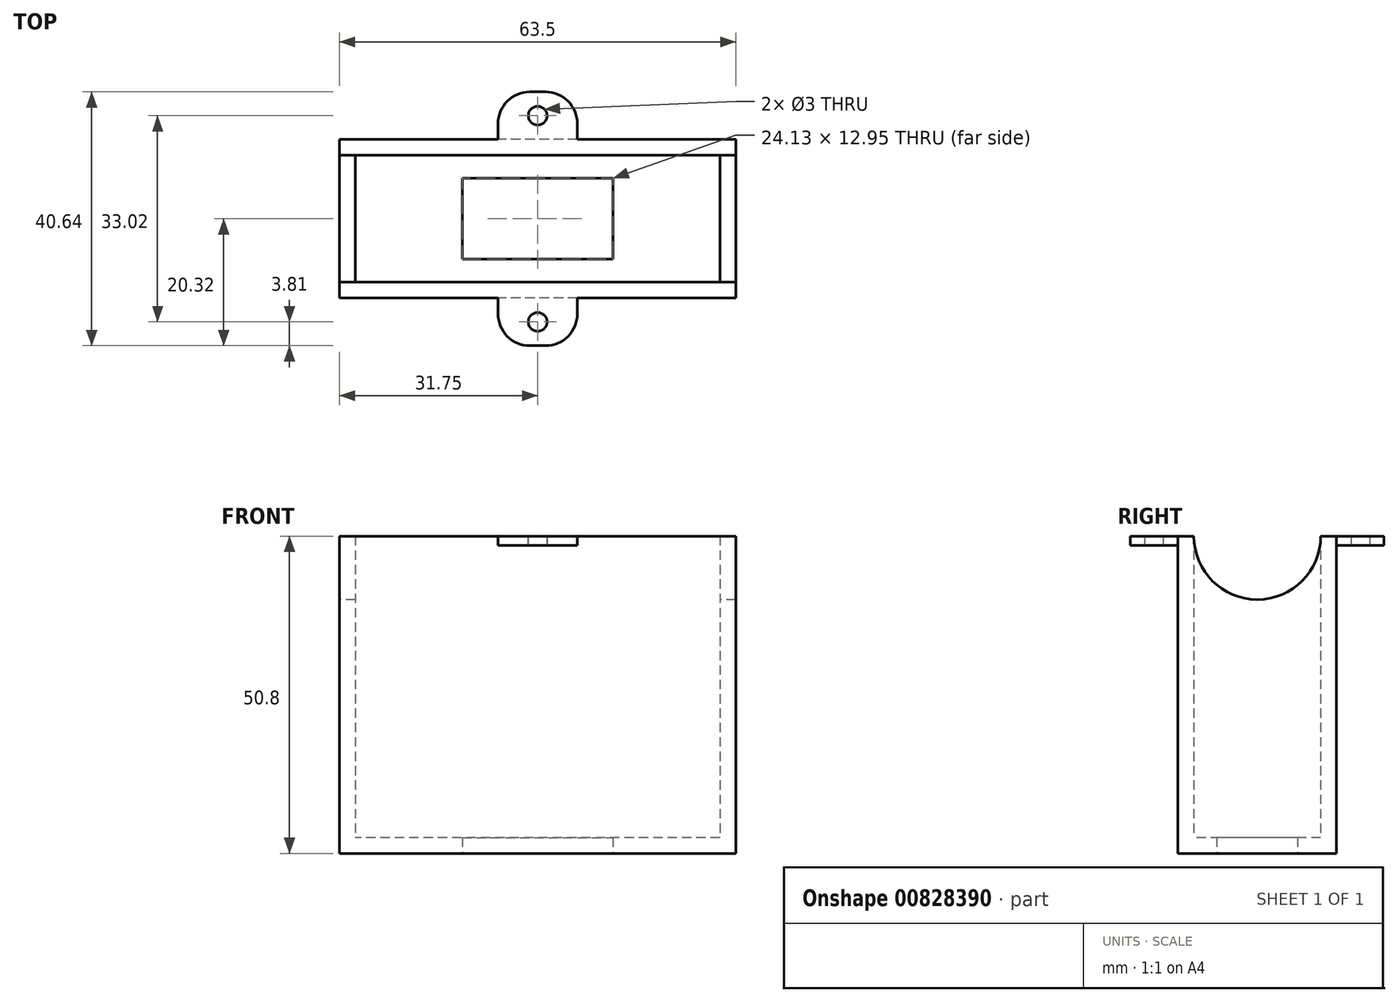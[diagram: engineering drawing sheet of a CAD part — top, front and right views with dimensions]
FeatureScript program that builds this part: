
annotation { "Feature Type Name" : "Feature", "Feature Type Description" : "" }
export const myFeature = defineFeature(function(context is Context, id is Id, definition is map)
    precondition{}
    {
        {
            var Q0;
            Q0=qCreatedBy(makeId("Top.planeOp"),FACE);
            var sketch = newSketch(context, id + "F0", { "sketchPlane" : qUnion([Q0])});
            skLineSegment(sketch, "E0.bottom", {"start": v(31.75, 12.7) * mm, "end": v(-31.75, 12.7) * mm});
            skLineSegment(sketch, "E0.top", {"start": v(31.75, -12.7) * mm, "end": v(-31.75, -12.7) * mm});
            skLineSegment(sketch, "E0.left", {"start": v(31.75, 12.7) * mm, "end": v(31.75, -12.7) * mm});
            skLineSegment(sketch, "E0.right", {"start": v(-31.75, 12.7) * mm, "end": v(-31.75, -12.7) * mm});
            skPoint(sketch, "E0.middle", {"position": v(0, 0) * mm});
            skLineSegment(sketch, "E1.bottom", {"start": v(29.21, 10.16) * mm, "end": v(-29.21, 10.16) * mm});
            skLineSegment(sketch, "E1.top", {"start": v(29.21, -10.16) * mm, "end": v(-29.21, -10.16) * mm});
            skLineSegment(sketch, "E1.left", {"start": v(29.21, 10.16) * mm, "end": v(29.21, -10.16) * mm});
            skLineSegment(sketch, "E1.right", {"start": v(-29.21, 10.16) * mm, "end": v(-29.21, -10.16) * mm});
            skSolve(sketch);
        }
        {
            var Q0;
            Q0 = qSketchRegion(id + "F0", true);
            extrude(context, id + "F1", {"entities" : qUnion([Q0]), "depth" : 50.8 * mm, "offsetDistance" : 25.4 * mm});
        }
        {
            var Q0;
            Q0=makeQuery(id+"F1.opExtrude","CAP_FACE",FACE,{"disambiguationData":[OSD([sQuery(id+"F0.wireOp",EDGE,"E0.bottom"),sQuery(id+"F0.wireOp",EDGE,"E0.top"),sQuery(id+"F0.wireOp",EDGE,"E0.left"),sQuery(id+"F0.wireOp",EDGE,"E0.right"),sQuery(id+"F0.wireOp",EDGE,"E1.bottom"),sQuery(id+"F0.wireOp",EDGE,"E1.top"),sQuery(id+"F0.wireOp",EDGE,"E1.left"),sQuery(id+"F0.wireOp",EDGE,"E1.right")])],"isStart":true});
            var sketch = newSketch(context, id + "F2", { "sketchPlane" : qUnion([Q0])});
            skLineSegment(sketch, "E2.bottom", {"start": v(29.21, -10.16) * mm, "end": v(-29.21, -10.16) * mm});
            skLineSegment(sketch, "E2.top", {"start": v(29.21, 10.16) * mm, "end": v(-29.21, 10.16) * mm});
            skLineSegment(sketch, "E2.left", {"start": v(29.21, -10.16) * mm, "end": v(29.21, 10.16) * mm});
            skLineSegment(sketch, "E2.right", {"start": v(-29.21, -10.16) * mm, "end": v(-29.21, 10.16) * mm});
            skPoint(sketch, "E2.middle", {"position": v(0, 0) * mm});
            skSolve(sketch);
        }
        {
            var Q0;
            Q0 = qSketchRegion(id + "F2", true);
            extrude(context, id + "F3", {"entities" : qUnion([Q0]), "operationType" : NewBodyOperationType.ADD, "oppositeDirection" : true, "depth" : 2.54 * mm, "offsetDistance" : 25.4 * mm});
        }
        {
            var Q0;
            Q0=makeQuery(id+"F1.opExtrude","SWEPT_FACE",FACE,{"disambiguationData":[OSD([sQuery(id+"F0.wireOp",EDGE,"E0.right")])]});
            var sketch = newSketch(context, id + "F4", { "sketchPlane" : qUnion([Q0])});
            skCircle(sketch, "E3", {"center": v(0, 50.8) * mm, "radius": 10.16 * mm});
            skSolve(sketch);
        }
        {
            var Q0;
            Q0 = qSketchRegion(id + "F4", true);
            extrude(context, id + "F5", {"entities" : qUnion([Q0]), "operationType" : NewBodyOperationType.REMOVE, "endBound" : BoundingType.THROUGH_ALL, "oppositeDirection" : true, "depth" : 25.4 * mm, "offsetDistance" : 25.4 * mm});
        }
        {
            var Q0;
            Q0=makeQuery(id+"F3.boolean.opBoolean","MERGE",FACE,{"derivedFrom":[makeQuery(id+"F1.opExtrude","CAP_FACE",FACE,{"disambiguationData":[OSD([sQuery(id+"F0.wireOp",EDGE,"E0.bottom"),sQuery(id+"F0.wireOp",EDGE,"E0.top"),sQuery(id+"F0.wireOp",EDGE,"E0.left"),sQuery(id+"F0.wireOp",EDGE,"E0.right"),sQuery(id+"F0.wireOp",EDGE,"E1.bottom"),sQuery(id+"F0.wireOp",EDGE,"E1.top"),sQuery(id+"F0.wireOp",EDGE,"E1.left"),sQuery(id+"F0.wireOp",EDGE,"E1.right")])],"isStart":true}),makeQuery(id+"F3.opExtrude","CAP_FACE",FACE,{"disambiguationData":[OSD([sQuery(id+"F2.wireOp",EDGE,"E2.bottom"),sQuery(id+"F2.wireOp",EDGE,"E2.top"),sQuery(id+"F2.wireOp",EDGE,"E2.left"),sQuery(id+"F2.wireOp",EDGE,"E2.right")])],"isStart":true})]});
            var sketch = newSketch(context, id + "F6", { "sketchPlane" : qUnion([Q0])});
            skLineSegment(sketch, "E4.bottom", {"start": v(-12.06, -6.48) * mm, "end": v(12.07, -6.48) * mm});
            skLineSegment(sketch, "E4.top", {"start": v(-12.07, 6.48) * mm, "end": v(12.06, 6.48) * mm});
            skLineSegment(sketch, "E4.left", {"start": v(-12.06, -6.48) * mm, "end": v(-12.07, 6.48) * mm});
            skLineSegment(sketch, "E4.right", {"start": v(12.07, -6.48) * mm, "end": v(12.06, 6.48) * mm});
            skPoint(sketch, "E4.middle", {"position": v(0, 0) * mm});
            skSolve(sketch);
        }
        {
            var Q0;
            Q0=makeQuery(id+"F1.opExtrude","SWEPT_FACE",FACE,{"disambiguationData":[OSD([sQuery(id+"F0.wireOp",EDGE,"E0.top")])]});
            var sketch = newSketch(context, id + "F7", { "sketchPlane" : qUnion([Q0])});
            skLineSegment(sketch, "E5.bottom", {"start": v(6.35, 50.8) * mm, "end": v(-6.35, 50.8) * mm});
            skLineSegment(sketch, "E5.top", {"start": v(6.35, 49.3) * mm, "end": v(-6.35, 49.3) * mm});
            skLineSegment(sketch, "E5.left", {"start": v(6.35, 50.8) * mm, "end": v(6.35, 49.3) * mm});
            skLineSegment(sketch, "E5.right", {"start": v(-6.35, 50.8) * mm, "end": v(-6.35, 49.3) * mm});
            skPoint(sketch, "E5.middle", {"position": v(0, 50.05) * mm});
            skSolve(sketch);
        }
        {
            var Q0;
            Q0 = qSketchRegion(id + "F7", true);
            extrude(context, id + "F8", {"entities" : qUnion([Q0]), "operationType" : NewBodyOperationType.ADD, "depth" : 7.62 * mm, "offsetDistance" : 25.4 * mm});
        }
        {
            var Q0;
            Q0=makeQuery(id+"F1.opExtrude","SWEPT_BODY",BODY,{"disambiguationData":[OSD([sQuery(id+"F0.wireOp",EDGE,"E0.bottom"),sQuery(id+"F0.wireOp",EDGE,"E0.top"),sQuery(id+"F0.wireOp",EDGE,"E0.left"),sQuery(id+"F0.wireOp",EDGE,"E0.right"),sQuery(id+"F0.wireOp",EDGE,"E1.bottom"),sQuery(id+"F0.wireOp",EDGE,"E1.top"),sQuery(id+"F0.wireOp",EDGE,"E1.left"),sQuery(id+"F0.wireOp",EDGE,"E1.right")])]});
            var Q1;
            Q1=qCreatedBy(makeId("Front.planeOp"),FACE);
            mirror(context, id + "F9", {"operationType" : NewBodyOperationType.ADD, "entities" : qUnion([Q0]), "mirrorPlane" : qUnion([Q1])});
        }
        {
            var Q0;
            {var subQ0=sQuery(id+"F0.wireOp",EDGE,"E1.top");var subQ1=sQuery(id+"F0.wireOp",EDGE,"E0.right");var subQ2=sQuery(id+"F0.wireOp",EDGE,"E0.left");var subQ3=sQuery(id+"F0.wireOp",EDGE,"E0.top");var subQ4=sQuery(id+"F0.wireOp",EDGE,"E1.left");var subQ5=sQuery(id+"F0.wireOp",EDGE,"E1.right");Q0=makeQuery(id+"F8.boolean.opBoolean","MERGE",FACE,{"derivedFrom":[makeQuery(id+"F5.boolean.opBoolean","SPLIT",FACE,{"disambiguationData":[TD([makeQuery(id+"F1.opExtrude","SWEPT_FACE",FACE,{"disambiguationData":[OSD([subQ3])]})])],"derivedFrom":makeQuery(id+"F1.opExtrude","CAP_FACE",FACE,{"disambiguationData":[OSD([sQuery(id+"F0.wireOp",EDGE,"E0.bottom"),subQ3,subQ2,subQ1,sQuery(id+"F0.wireOp",EDGE,"E1.bottom"),subQ0,subQ4,subQ5])],"isStart":false})}),makeQuery(id+"F8.opExtrude","SWEPT_FACE",FACE,{"disambiguationData":[OSD([sQuery(id+"F7.wireOp",EDGE,"E5.bottom")])]})]});}
            var sketch = newSketch(context, id + "F10", { "sketchPlane" : qUnion([Q0])});
            skCircle(sketch, "E6", {"center": v(0, -16.51) * mm, "radius": 1.5 * mm});
            skPoint(sketch, "E6.centerSnap0", {"position": v(6.35, -16.51) * mm});
            skPoint(sketch, "E6.centerSnap1", {"position": v(0, -20.32) * mm});
            skSolve(sketch);
        }
        {
            var Q0;
            Q0 = qSketchRegion(id + "F10", true);
            extrude(context, id + "F11", {"entities" : qUnion([Q0]), "operationType" : NewBodyOperationType.REMOVE, "oppositeDirection" : true, "depth" : 25.4 * mm, "offsetDistance" : 25.4 * mm});
        }
        {
            var Q0;
            Q0=makeQuery(id+"F9.opPattern","COPY",FACE,{"derivedFrom":makeQuery(id+"F8.opExtrude","SWEPT_FACE",FACE,{"disambiguationData":[OSD([sQuery(id+"F7.wireOp",EDGE,"E5.top")])]}),"instanceName":"1"});
            var sketch = newSketch(context, id + "F12", { "sketchPlane" : qUnion([Q0])});
            skCircle(sketch, "E7", {"center": v(0, -16.51) * mm, "radius": 1.5 * mm});
            skPoint(sketch, "E8", {"position": v(6.35, -16.51) * mm});
            skLineSegment(sketch, "E9", {"start": v(6.35, -16.51) * mm, "end": v(0, -16.51) * mm});
            skSolve(sketch);
        }
        {
            var Q0;
            Q0=makeQuery(id+"F12.imprint","IMPRINT",FACE,{"disambiguationData":[TD([[makeQuery(id+"F12.imprint","IMPRINT",EDGE,{"derivedFrom":sQuery(id+"F12.wireOp",EDGE,"E7")}),1.0]])]});
            extrude(context, id + "F13", {"entities" : qUnion([Q0]), "operationType" : NewBodyOperationType.REMOVE, "oppositeDirection" : true, "depth" : 25.4 * mm, "offsetDistance" : 25.4 * mm});
        }
        {
            var Q0;
            Q0=makeQuery(id+"F9.opPattern","COPY",EDGE,{"derivedFrom":makeQuery(id+"F8.opExtrude","CAP_EDGE",EDGE,{"disambiguationData":[OSD([sQuery(id+"F7.wireOp",EDGE,"E5.left")])],"isStart":false}),"instanceName":"1"});
            var Q1;
            Q1=makeQuery(id+"F9.opPattern","COPY",EDGE,{"derivedFrom":makeQuery(id+"F8.opExtrude","CAP_EDGE",EDGE,{"disambiguationData":[OSD([sQuery(id+"F7.wireOp",EDGE,"E5.right")])],"isStart":false}),"instanceName":"1"});
            var Q2;
            Q2=makeQuery(id+"F8.opExtrude","CAP_EDGE",EDGE,{"disambiguationData":[OSD([sQuery(id+"F7.wireOp",EDGE,"E5.left")])],"isStart":false});
            var Q3;
            Q3=makeQuery(id+"F8.opExtrude","CAP_EDGE",EDGE,{"disambiguationData":[OSD([sQuery(id+"F7.wireOp",EDGE,"E5.right")])],"isStart":false});
            fillet(context, id + "F14", {"entities" : qUnion([Q0, Q1, Q2, Q3]), "radius" : 5.08 * mm, "tangentPropagation" : true, "allowEdgeOverflow" : false});
        }
        {
            var Q0;
            Q0=makeQuery(id+"F6.imprint","IMPRINT",FACE,{"disambiguationData":[TD([[makeQuery(id+"F6.imprint","IMPRINT",EDGE,{"derivedFrom":sQuery(id+"F6.wireOp",EDGE,"E4.bottom")}),1.0]])]});
            extrude(context, id + "F15", {"entities" : qUnion([Q0]), "operationType" : NewBodyOperationType.REMOVE, "oppositeDirection" : true, "depth" : 25.4 * mm, "offsetDistance" : 25.4 * mm});
        }
    });
